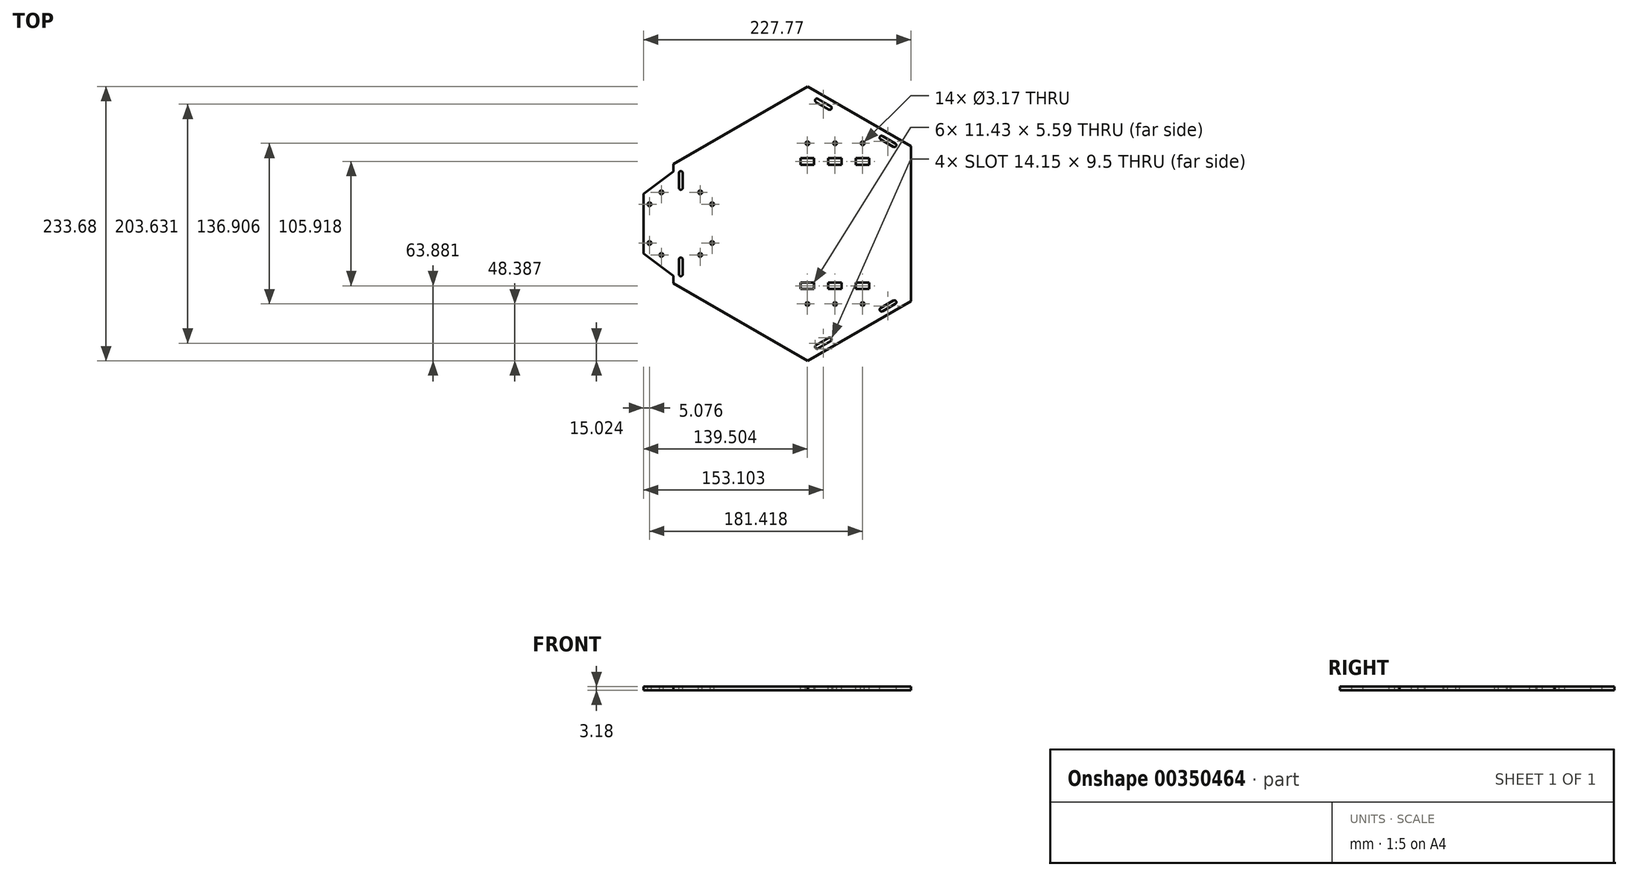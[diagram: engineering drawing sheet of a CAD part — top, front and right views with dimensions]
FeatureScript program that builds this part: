
annotation { "Feature Type Name" : "Feature", "Feature Type Description" : "" }
export const myFeature = defineFeature(function(context is Context, id is Id, definition is map)
    precondition{}
    {
        {
            var Q0;
            Q0=qCreatedBy(makeId("Top.planeOp"),FACE);
            var sketch = newSketch(context, id + "F0", { "sketchPlane" : qUnion([Q0])});
            skLineSegment(sketch, "E0", {"start": v(-105.22, -19.05) * mm, "end": v(-105.22, -69.85) * mm});
            skLineSegment(sketch, "E1", {"start": v(-105.22, -69.85) * mm, "end": v(-79.82, -88.9) * mm});
            skLineSegment(sketch, "E2", {"start": v(-79.82, -88.9) * mm, "end": v(-79.82, -95.25) * mm});
            skLineSegment(sketch, "E3", {"start": v(-79.82, -95.25) * mm, "end": v(34.56, -161.29) * mm});
            skLineSegment(sketch, "E4", {"start": v(34.56, -161.29) * mm, "end": v(122.55, -110.49) * mm});
            skLineSegment(sketch, "E5", {"start": v(122.55, -110.49) * mm, "end": v(122.55, 21.6) * mm});
            skLineSegment(sketch, "E6", {"start": v(122.55, 21.6) * mm, "end": v(34.56, 72.4) * mm});
            skLineSegment(sketch, "E7", {"start": v(34.56, 72.4) * mm, "end": v(-79.82, 6.35) * mm});
            skLineSegment(sketch, "E8", {"start": v(-79.82, 6.35) * mm, "end": v(-79.82, 0) * mm});
            skLineSegment(sketch, "E9", {"start": v(-79.82, 0) * mm, "end": v(-105.22, -19.05) * mm});
            skCircle(sketch, "E10.cCircle", {"center": v(0, 0) * mm, "radius": 98.99 * mm, "construction": true});
            skLineSegment(sketch, "E10.0", {"start": v(-98.99, -171.45) * mm, "end": v(-98.99, 171.45) * mm, "construction": true});
            skLineSegment(sketch, "E10.1", {"start": v(-98.99, 171.45) * mm, "end": v(197.97, 0) * mm, "construction": true});
            skLineSegment(sketch, "E10.2", {"start": v(197.97, 0) * mm, "end": v(-98.99, -171.45) * mm, "construction": true});
            skPoint(sketch, "E10.0.midPoint", {"position": v(-98.99, 0) * mm});
            skSolve(sketch);
        }
        {
            var Q0;
            Q0=makeQuery(id+"F0.imprint","IMPRINT",FACE,{"disambiguationData":[TD([[makeQuery(id+"F0.imprint","IMPRINT",EDGE,{"derivedFrom":sQuery(id+"F0.wireOp",EDGE,"E0")}),1.0]])]});
            extrude(context, id + "F1", {"entities" : qUnion([Q0]), "depth" : 3.17 * mm});
        }
        {
            var Q0;
            Q0=makeQuery(id+"F1.opExtrude","CAP_FACE",FACE,{"disambiguationData":[OSD([sQuery(id+"F0.wireOp",EDGE,"E0"),sQuery(id+"F0.wireOp",EDGE,"E1"),sQuery(id+"F0.wireOp",EDGE,"E2"),sQuery(id+"F0.wireOp",EDGE,"E3"),sQuery(id+"F0.wireOp",EDGE,"E4"),sQuery(id+"F0.wireOp",EDGE,"E5"),sQuery(id+"F0.wireOp",EDGE,"E6"),sQuery(id+"F0.wireOp",EDGE,"E7"),sQuery(id+"F0.wireOp",EDGE,"E8"),sQuery(id+"F0.wireOp",EDGE,"E9")])],"isStart":false});
            var sketch = newSketch(context, id + "F2", { "sketchPlane" : qUnion([Q0])});
            skLineSegment(sketch, "E11", {"start": v(34.56, 72.4) * mm, "end": v(31.39, 66.9) * mm, "construction": true});
            skLineSegment(sketch, "E12", {"start": v(31.39, 66.9) * mm, "end": v(119.37, 16.1) * mm, "construction": true});
            skLineSegment(sketch, "E13", {"start": v(119.37, 16.1) * mm, "end": v(122.55, 21.6) * mm, "construction": true});
            skArc(sketch, "E14", {"start": v(43.18, 61.92) * mm, "mid": v(41, 61.33) * mm, "end": v(41.6, 59.17) * mm});
            skArc(sketch, "E15", {"start": v(52.59, 52.82) * mm, "mid": v(54.76, 53.4) * mm, "end": v(54.18, 55.57) * mm});
            skArc(sketch, "E16", {"start": v(107.58, 21.07) * mm, "mid": v(109.75, 21.65) * mm, "end": v(109.17, 23.82) * mm});
            skArc(sketch, "E17", {"start": v(98.17, 30.17) * mm, "mid": v(96, 29.58) * mm, "end": v(96.58, 27.42) * mm});
            skLineSegment(sketch, "E18", {"start": v(43.18, 61.92) * mm, "end": v(54.18, 55.57) * mm});
            skLineSegment(sketch, "E19", {"start": v(41.6, 59.17) * mm, "end": v(52.59, 52.82) * mm});
            skLineSegment(sketch, "E20", {"start": v(98.17, 30.17) * mm, "end": v(109.17, 23.82) * mm});
            skLineSegment(sketch, "E21", {"start": v(96.58, 27.42) * mm, "end": v(107.58, 21.07) * mm});
            skLineSegment(sketch, "E22", {"start": v(34.56, -161.29) * mm, "end": v(31.39, -155.8) * mm, "construction": true});
            skLineSegment(sketch, "E23", {"start": v(31.39, -155.8) * mm, "end": v(119.37, -105) * mm, "construction": true});
            skLineSegment(sketch, "E24", {"start": v(119.37, -105) * mm, "end": v(122.55, -110.49) * mm, "construction": true});
            skArc(sketch, "E25", {"start": v(41.6, -148.07) * mm, "mid": v(41, -150.23) * mm, "end": v(43.18, -150.82) * mm});
            skArc(sketch, "E26", {"start": v(54.18, -144.47) * mm, "mid": v(54.76, -142.3) * mm, "end": v(52.59, -141.72) * mm});
            skCircle(sketch, "E27", {"center": v(108.38, -111.34) * mm, "radius": 1.59 * mm});
            skCircle(sketch, "E28", {"center": v(97.38, -117.7) * mm, "radius": 1.59 * mm});
            skLineSegment(sketch, "E29", {"start": v(41.6, -148.07) * mm, "end": v(52.59, -141.72) * mm});
            skLineSegment(sketch, "E30", {"start": v(54.18, -144.47) * mm, "end": v(43.18, -150.82) * mm});
            skLineSegment(sketch, "E31", {"start": v(98.17, -119.07) * mm, "end": v(109.17, -112.72) * mm});
            skLineSegment(sketch, "E32", {"start": v(96.58, -116.32) * mm, "end": v(107.58, -109.97) * mm});
            skLineSegment(sketch, "E33", {"start": v(-79.82, 6.35) * mm, "end": v(-73.47, 6.35) * mm, "construction": true});
            skLineSegment(sketch, "E34", {"start": v(-73.47, 6.35) * mm, "end": v(-73.47, -95.25) * mm, "construction": true});
            skLineSegment(sketch, "E35", {"start": v(-73.47, -95.25) * mm, "end": v(-79.82, -95.25) * mm, "construction": true});
            skArc(sketch, "E36", {"start": v(-71.89, -1.27) * mm, "mid": v(-73.47, 0.32) * mm, "end": v(-75.06, -1.27) * mm});
            skArc(sketch, "E37", {"start": v(-75.06, -13.97) * mm, "mid": v(-73.47, -15.56) * mm, "end": v(-71.89, -13.97) * mm});
            skArc(sketch, "E38", {"start": v(-75.06, -87.63) * mm, "mid": v(-73.47, -89.22) * mm, "end": v(-71.89, -87.63) * mm});
            skArc(sketch, "E39", {"start": v(-71.89, -74.93) * mm, "mid": v(-73.47, -73.34) * mm, "end": v(-75.06, -74.93) * mm});
            skLineSegment(sketch, "E40", {"start": v(-75.06, -74.93) * mm, "end": v(-75.06, -87.63) * mm});
            skLineSegment(sketch, "E41", {"start": v(-71.89, -74.93) * mm, "end": v(-71.89, -87.63) * mm});
            skLineSegment(sketch, "E42", {"start": v(-75.06, -1.27) * mm, "end": v(-75.06, -13.97) * mm});
            skLineSegment(sketch, "E43", {"start": v(-71.89, -1.27) * mm, "end": v(-71.89, -13.97) * mm});
            skPoint(sketch, "E44", {"position": v(122.55, 5.72) * mm});
            skPoint(sketch, "E45", {"position": v(122.55, -94.61) * mm});
            skLineSegment(sketch, "E46", {"start": v(122.55, 5.72) * mm, "end": v(20.95, 5.72) * mm, "construction": true});
            skLineSegment(sketch, "E47", {"start": v(20.95, 11.3) * mm, "end": v(122.55, 11.3) * mm, "construction": true});
            skPoint(sketch, "E48", {"position": v(28.57, 11.3) * mm});
            skPoint(sketch, "E49", {"position": v(40, 11.3) * mm});
            skPoint(sketch, "E50", {"position": v(52.06, 11.3) * mm});
            skPoint(sketch, "E51", {"position": v(63.5, 11.3) * mm});
            skPoint(sketch, "E52", {"position": v(75.56, 11.3) * mm});
            skPoint(sketch, "E53", {"position": v(86.99, 11.3) * mm});
            skLineSegment(sketch, "E54", {"start": v(86.99, 11.3) * mm, "end": v(86.99, 5.72) * mm});
            skLineSegment(sketch, "E55", {"start": v(75.56, 11.3) * mm, "end": v(75.56, 5.72) * mm});
            skLineSegment(sketch, "E56", {"start": v(63.5, 11.3) * mm, "end": v(63.5, 5.72) * mm});
            skLineSegment(sketch, "E57", {"start": v(52.06, 11.3) * mm, "end": v(52.06, 5.72) * mm});
            skLineSegment(sketch, "E58", {"start": v(28.57, 11.3) * mm, "end": v(28.57, 5.72) * mm});
            skLineSegment(sketch, "E59", {"start": v(40, 11.3) * mm, "end": v(40, 5.72) * mm});
            skLineSegment(sketch, "E60", {"start": v(20.95, 5.72) * mm, "end": v(20.95, 11.3) * mm, "construction": true});
            skLineSegment(sketch, "E61", {"start": v(122.55, -94.61) * mm, "end": v(20.95, -94.61) * mm, "construction": true});
            skLineSegment(sketch, "E62", {"start": v(20.95, -100.2) * mm, "end": v(122.55, -100.2) * mm, "construction": true});
            skLineSegment(sketch, "E63", {"start": v(20.95, -94.61) * mm, "end": v(20.95, -100.2) * mm, "construction": true});
            skPoint(sketch, "E64", {"position": v(28.57, -100.2) * mm});
            skPoint(sketch, "E65", {"position": v(40, -100.2) * mm});
            skPoint(sketch, "E66", {"position": v(52.06, -100.2) * mm});
            skPoint(sketch, "E67", {"position": v(63.5, -100.2) * mm});
            skPoint(sketch, "E68", {"position": v(75.56, -100.2) * mm});
            skPoint(sketch, "E69", {"position": v(86.99, -100.2) * mm});
            skLineSegment(sketch, "E70", {"start": v(28.57, -100.2) * mm, "end": v(28.57, -94.61) * mm});
            skLineSegment(sketch, "E71", {"start": v(40, -100.2) * mm, "end": v(40, -94.61) * mm});
            skLineSegment(sketch, "E72", {"start": v(52.06, -100.2) * mm, "end": v(52.06, -94.61) * mm});
            skLineSegment(sketch, "E73", {"start": v(63.5, -100.2) * mm, "end": v(63.5, -94.61) * mm});
            skLineSegment(sketch, "E74", {"start": v(75.56, -100.2) * mm, "end": v(75.56, -94.61) * mm});
            skLineSegment(sketch, "E75", {"start": v(86.99, -100.2) * mm, "end": v(86.99, -94.61) * mm});
            skLineSegment(sketch, "E76", {"start": v(28.57, 11.3) * mm, "end": v(40, 11.3) * mm});
            skLineSegment(sketch, "E77", {"start": v(28.57, 5.72) * mm, "end": v(40, 5.72) * mm});
            skLineSegment(sketch, "E78", {"start": v(52.06, 11.3) * mm, "end": v(63.5, 11.3) * mm});
            skLineSegment(sketch, "E79", {"start": v(52.06, 5.72) * mm, "end": v(63.5, 5.72) * mm});
            skLineSegment(sketch, "E80", {"start": v(75.56, 11.3) * mm, "end": v(86.99, 11.3) * mm});
            skLineSegment(sketch, "E81", {"start": v(75.56, 5.72) * mm, "end": v(86.99, 5.72) * mm});
            skLineSegment(sketch, "E82", {"start": v(28.57, -94.61) * mm, "end": v(40, -94.61) * mm});
            skLineSegment(sketch, "E83", {"start": v(28.57, -100.2) * mm, "end": v(40, -100.2) * mm});
            skLineSegment(sketch, "E84", {"start": v(52.06, -94.61) * mm, "end": v(63.5, -94.61) * mm});
            skLineSegment(sketch, "E85", {"start": v(52.06, -100.2) * mm, "end": v(63.5, -100.2) * mm});
            skLineSegment(sketch, "E86", {"start": v(75.56, -94.61) * mm, "end": v(86.99, -94.61) * mm});
            skLineSegment(sketch, "E87", {"start": v(75.56, -100.2) * mm, "end": v(86.99, -100.2) * mm});
            skPoint(sketch, "E88", {"position": v(34.28, -100.2) * mm});
            skPoint(sketch, "E89", {"position": v(57.78, -100.2) * mm});
            skPoint(sketch, "E90", {"position": v(81.27, -100.2) * mm});
            skLineSegment(sketch, "E91", {"start": v(34.28, -100.2) * mm, "end": v(34.28, -112.9) * mm, "construction": true});
            skLineSegment(sketch, "E92", {"start": v(57.78, -100.2) * mm, "end": v(57.78, -112.9) * mm, "construction": true});
            skLineSegment(sketch, "E93", {"start": v(81.27, -100.2) * mm, "end": v(81.27, -112.9) * mm, "construction": true});
            skPoint(sketch, "E94", {"position": v(34.28, 11.3) * mm});
            skPoint(sketch, "E95", {"position": v(57.78, 11.3) * mm});
            skPoint(sketch, "E96", {"position": v(81.27, 11.3) * mm});
            skLineSegment(sketch, "E97", {"start": v(34.28, 11.3) * mm, "end": v(34.28, 24) * mm, "construction": true});
            skLineSegment(sketch, "E98", {"start": v(57.78, 11.3) * mm, "end": v(57.78, 24) * mm, "construction": true});
            skLineSegment(sketch, "E99", {"start": v(81.27, 11.3) * mm, "end": v(81.27, 24) * mm, "construction": true});
            skCircle(sketch, "E100", {"center": v(34.28, 24) * mm, "radius": 1.59 * mm});
            skCircle(sketch, "E101", {"center": v(57.78, 24) * mm, "radius": 1.59 * mm});
            skCircle(sketch, "E102", {"center": v(81.27, 24) * mm, "radius": 1.59 * mm});
            skCircle(sketch, "E103", {"center": v(34.28, -112.9) * mm, "radius": 1.59 * mm});
            skCircle(sketch, "E104", {"center": v(57.78, -112.9) * mm, "radius": 1.59 * mm});
            skCircle(sketch, "E105", {"center": v(81.27, -112.9) * mm, "radius": 1.59 * mm});
            skPoint(sketch, "E106", {"position": v(-105.22, -44.45) * mm});
            skLineSegment(sketch, "E107", {"start": v(-105.22, -44.45) * mm, "end": v(-73.47, -44.45) * mm, "construction": true});
            skPoint(sketch, "E108", {"position": v(-73.47, -22.86) * mm});
            skPoint(sketch, "E109", {"position": v(-73.47, -66.04) * mm});
            skLineSegment(sketch, "E110", {"start": v(-73.47, -44.45) * mm, "end": v(-51.88, -44.45) * mm, "construction": true});
            skPoint(sketch, "E111", {"position": v(-95.06, -44.45) * mm});
            skLineSegment(sketch, "E112", {"start": v(-95.06, -22.86) * mm, "end": v(-51.88, -22.86) * mm});
            skLineSegment(sketch, "E113", {"start": v(-95.06, -22.86) * mm, "end": v(-95.06, -66.04) * mm});
            skLineSegment(sketch, "E114", {"start": v(-95.06, -66.04) * mm, "end": v(-51.88, -66.04) * mm});
            skLineSegment(sketch, "E115", {"start": v(-51.88, -22.86) * mm, "end": v(-51.88, -44.45) * mm});
            skLineSegment(sketch, "E116", {"start": v(-51.88, -44.45) * mm, "end": v(-51.88, -66.04) * mm});
            skLineSegment(sketch, "E117", {"start": v(-95.06, -71.12) * mm, "end": v(-51.88, -71.12) * mm, "construction": true});
            skLineSegment(sketch, "E118", {"start": v(-100.14, -66.04) * mm, "end": v(-100.14, -22.86) * mm, "construction": true});
            skLineSegment(sketch, "E119", {"start": v(-95.06, -17.78) * mm, "end": v(-51.88, -17.78) * mm, "construction": true});
            skLineSegment(sketch, "E120", {"start": v(-46.8, -22.86) * mm, "end": v(-46.8, -66.04) * mm, "construction": true});
            skPoint(sketch, "E121", {"position": v(-73.47, -17.78) * mm});
            skPoint(sketch, "E122", {"position": v(-100.14, -44.45) * mm});
            skPoint(sketch, "E123", {"position": v(-73.47, -71.12) * mm});
            skLineSegment(sketch, "E124", {"start": v(-51.88, -44.45) * mm, "end": v(-46.8, -44.45) * mm, "construction": true});
            skCircle(sketch, "E125", {"center": v(-100.14, -60.96) * mm, "radius": 1.59 * mm});
            skCircle(sketch, "E126", {"center": v(-100.14, -27.94) * mm, "radius": 1.59 * mm});
            skCircle(sketch, "E127", {"center": v(-89.98, -17.78) * mm, "radius": 1.59 * mm});
            skCircle(sketch, "E128", {"center": v(-56.96, -17.78) * mm, "radius": 1.59 * mm});
            skCircle(sketch, "E129", {"center": v(-46.8, -27.94) * mm, "radius": 1.59 * mm});
            skCircle(sketch, "E130", {"center": v(-46.8, -60.96) * mm, "radius": 1.59 * mm});
            skCircle(sketch, "E131", {"center": v(-56.96, -71.12) * mm, "radius": 1.59 * mm});
            skCircle(sketch, "E132", {"center": v(-89.98, -71.12) * mm, "radius": 1.59 * mm});
            skSolve(sketch);
        }
        {
            var Q0;
            Q0=makeQuery(id+"F2.imprint","IMPRINT",FACE,{"disambiguationData":[TD([[makeQuery(id+"F2.imprint","IMPRINT",EDGE,{"derivedFrom":sQuery(id+"F2.wireOp",EDGE,"E126")}),1.0]])]});
            var Q1;
            Q1=makeQuery(id+"F2.imprint","IMPRINT",FACE,{"disambiguationData":[TD([[makeQuery(id+"F2.imprint","IMPRINT",EDGE,{"derivedFrom":sQuery(id+"F2.wireOp",EDGE,"E127")}),1.0]])]});
            var Q2;
            Q2=makeQuery(id+"F2.imprint","IMPRINT",FACE,{"disambiguationData":[TD([[makeQuery(id+"F2.imprint","IMPRINT",EDGE,{"derivedFrom":sQuery(id+"F2.wireOp",EDGE,"E128")}),1.0]])]});
            var Q3;
            Q3=makeQuery(id+"F2.imprint","IMPRINT",FACE,{"disambiguationData":[TD([[makeQuery(id+"F2.imprint","IMPRINT",EDGE,{"derivedFrom":sQuery(id+"F2.wireOp",EDGE,"E129")}),1.0]])]});
            var Q4;
            Q4=makeQuery(id+"F2.imprint","IMPRINT",FACE,{"disambiguationData":[TD([[makeQuery(id+"F2.imprint","IMPRINT",EDGE,{"derivedFrom":sQuery(id+"F2.wireOp",EDGE,"E130")}),1.0]])]});
            var Q5;
            Q5=makeQuery(id+"F2.imprint","IMPRINT",FACE,{"disambiguationData":[TD([[makeQuery(id+"F2.imprint","IMPRINT",EDGE,{"derivedFrom":sQuery(id+"F2.wireOp",EDGE,"E131")}),1.0]])]});
            var Q6;
            Q6=makeQuery(id+"F2.imprint","IMPRINT",FACE,{"disambiguationData":[TD([[makeQuery(id+"F2.imprint","IMPRINT",EDGE,{"derivedFrom":sQuery(id+"F2.wireOp",EDGE,"E132")}),1.0]])]});
            var Q7;
            Q7=makeQuery(id+"F2.imprint","IMPRINT",FACE,{"disambiguationData":[TD([[makeQuery(id+"F2.imprint","IMPRINT",EDGE,{"derivedFrom":sQuery(id+"F2.wireOp",EDGE,"E125")}),1.0]])]});
            var Q8;
            Q8=makeQuery(id+"F2.imprint","IMPRINT",FACE,{"disambiguationData":[TD([[makeQuery(id+"F2.imprint","IMPRINT",EDGE,{"derivedFrom":sQuery(id+"F2.wireOp",EDGE,"E38")}),1.0]])]});
            var Q9;
            Q9=makeQuery(id+"F2.imprint","IMPRINT",FACE,{"disambiguationData":[TD([[makeQuery(id+"F2.imprint","IMPRINT",EDGE,{"derivedFrom":sQuery(id+"F2.wireOp",EDGE,"E36")}),1.0]])]});
            var Q10;
            Q10=makeQuery(id+"F2.imprint","IMPRINT",FACE,{"disambiguationData":[TD([[makeQuery(id+"F2.imprint","IMPRINT",EDGE,{"derivedFrom":sQuery(id+"F2.wireOp",EDGE,"E58")}),1.0]])]});
            var Q11;
            Q11=makeQuery(id+"F2.imprint","IMPRINT",FACE,{"disambiguationData":[TD([[makeQuery(id+"F2.imprint","IMPRINT",EDGE,{"derivedFrom":sQuery(id+"F2.wireOp",EDGE,"E56")}),-1.0]])]});
            var Q12;
            Q12=makeQuery(id+"F2.imprint","IMPRINT",FACE,{"disambiguationData":[TD([[makeQuery(id+"F2.imprint","IMPRINT",EDGE,{"derivedFrom":sQuery(id+"F2.wireOp",EDGE,"E54")}),-1.0]])]});
            var Q13;
            Q13=makeQuery(id+"F2.imprint","IMPRINT",FACE,{"disambiguationData":[TD([[makeQuery(id+"F2.imprint","IMPRINT",EDGE,{"derivedFrom":sQuery(id+"F2.wireOp",EDGE,"E101")}),1.0]])]});
            var Q14;
            Q14=makeQuery(id+"F2.imprint","IMPRINT",FACE,{"disambiguationData":[TD([[makeQuery(id+"F2.imprint","IMPRINT",EDGE,{"derivedFrom":sQuery(id+"F2.wireOp",EDGE,"E100")}),1.0]])]});
            var Q15;
            Q15=makeQuery(id+"F2.imprint","IMPRINT",FACE,{"disambiguationData":[TD([[makeQuery(id+"F2.imprint","IMPRINT",EDGE,{"derivedFrom":sQuery(id+"F2.wireOp",EDGE,"E74")}),-1.0]])]});
            var Q16;
            Q16=makeQuery(id+"F2.imprint","IMPRINT",FACE,{"disambiguationData":[TD([[makeQuery(id+"F2.imprint","IMPRINT",EDGE,{"derivedFrom":sQuery(id+"F2.wireOp",EDGE,"E72")}),-1.0]])]});
            var Q17;
            Q17=makeQuery(id+"F2.imprint","IMPRINT",FACE,{"disambiguationData":[TD([[makeQuery(id+"F2.imprint","IMPRINT",EDGE,{"derivedFrom":sQuery(id+"F2.wireOp",EDGE,"E70")}),-1.0]])]});
            var Q18;
            Q18=makeQuery(id+"F2.imprint","IMPRINT",FACE,{"disambiguationData":[TD([[makeQuery(id+"F2.imprint","IMPRINT",EDGE,{"derivedFrom":sQuery(id+"F2.wireOp",EDGE,"E103")}),1.0]])]});
            var Q19;
            Q19=makeQuery(id+"F2.imprint","IMPRINT",FACE,{"disambiguationData":[TD([[makeQuery(id+"F2.imprint","IMPRINT",EDGE,{"derivedFrom":sQuery(id+"F2.wireOp",EDGE,"E104")}),1.0]])]});
            var Q20;
            Q20=makeQuery(id+"F2.imprint","IMPRINT",FACE,{"disambiguationData":[TD([[makeQuery(id+"F2.imprint","IMPRINT",EDGE,{"derivedFrom":sQuery(id+"F2.wireOp",EDGE,"E105")}),1.0]])]});
            var Q21;
            {var subQ0=sQuery(id+"F2.wireOp",EDGE,"E31");Q21=makeQuery(id+"F2.imprint","IMPRINT",FACE,{"disambiguationData":[TD([[makeQuery(id+"F2.imprint","IMPRINT",EDGE,{"derivedFrom":subQ0}),1.0]])]});}
            var Q22;
            {var subQ0=sQuery(id+"F2.wireOp",EDGE,"E28");var subQ1=makeQuery(id+"F2.imprint","INTERSECT",VERTEX,{"derivedFrom":[subQ0,sQuery(id+"F2.wireOp",EDGE,"E31")]});Q22=makeQuery(id+"F2.imprint","IMPRINT",FACE,{"disambiguationData":[TD([[makeQuery(id+"F2.imprint","IMPRINT",EDGE,{"disambiguationData":[TD([[subQ1,1.0]])],"derivedFrom":subQ0}),1.0]])]});}
            var Q23;
            {var subQ0=sQuery(id+"F2.wireOp",EDGE,"E27");var subQ1=makeQuery(id+"F2.imprint","INTERSECT",VERTEX,{"derivedFrom":[subQ0,sQuery(id+"F2.wireOp",EDGE,"E31")]});Q23=makeQuery(id+"F2.imprint","IMPRINT",FACE,{"disambiguationData":[TD([[makeQuery(id+"F2.imprint","IMPRINT",EDGE,{"disambiguationData":[TD([[subQ1,1.0]])],"derivedFrom":subQ0}),1.0]])]});}
            var Q24;
            Q24=makeQuery(id+"F2.imprint","IMPRINT",FACE,{"disambiguationData":[TD([[makeQuery(id+"F2.imprint","IMPRINT",EDGE,{"derivedFrom":sQuery(id+"F2.wireOp",EDGE,"E25")}),1.0]])]});
            var Q25;
            Q25=makeQuery(id+"F2.imprint","IMPRINT",FACE,{"disambiguationData":[TD([[makeQuery(id+"F2.imprint","IMPRINT",EDGE,{"derivedFrom":sQuery(id+"F2.wireOp",EDGE,"E16")}),1.0]])]});
            var Q26;
            Q26=makeQuery(id+"F2.imprint","IMPRINT",FACE,{"disambiguationData":[TD([[makeQuery(id+"F2.imprint","IMPRINT",EDGE,{"derivedFrom":sQuery(id+"F2.wireOp",EDGE,"E14")}),1.0]])]});
            var Q27;
            Q27=makeQuery(id+"F2.imprint","IMPRINT",FACE,{"disambiguationData":[TD([[makeQuery(id+"F2.imprint","IMPRINT",EDGE,{"derivedFrom":sQuery(id+"F2.wireOp",EDGE,"E102")}),1.0]])]});
            extrude(context, id + "F3", {"entities" : qUnion([Q0, Q1, Q2, Q3, Q4, Q5, Q6, Q7, Q8, Q9, Q10, Q11, Q12, Q13, Q14, Q15, Q16, Q17, Q18, Q19, Q20, Q21, Q22, Q23, Q24, Q25, Q26, Q27]), "operationType" : NewBodyOperationType.REMOVE, "oppositeDirection" : true, "depth" : 25.4 * mm});
        }
    });
